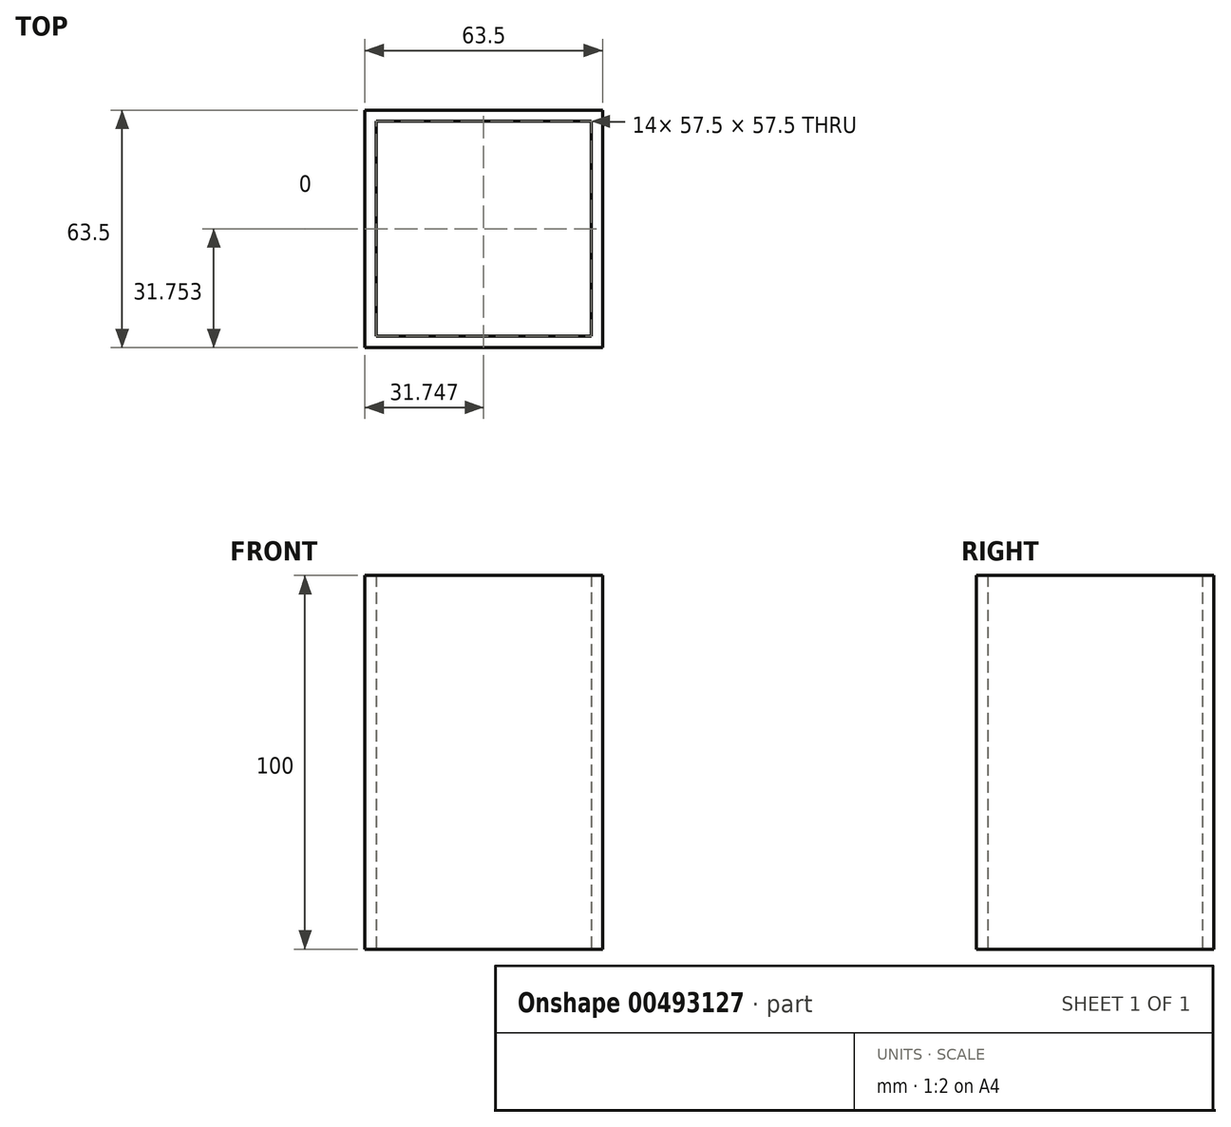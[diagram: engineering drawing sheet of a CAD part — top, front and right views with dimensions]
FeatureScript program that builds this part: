
annotation { "Feature Type Name" : "Feature", "Feature Type Description" : "" }
export const myFeature = defineFeature(function(context is Context, id is Id, definition is map)
    precondition{}
    {
        {
            var Q0;
            Q0=qCreatedBy(makeId("Top.planeOp"),FACE);
            var sketch = newSketch(context, id + "F0", { "sketchPlane" : qUnion([Q0])});
            skLineSegment(sketch, "E0.bottom", {"start": v(-27.63, 16.07) * mm, "end": v(29.87, 16.07) * mm});
            skLineSegment(sketch, "E0.top", {"start": v(-27.63, -41.43) * mm, "end": v(29.87, -41.43) * mm});
            skLineSegment(sketch, "E0.left", {"start": v(-27.63, 16.07) * mm, "end": v(-27.63, -41.43) * mm});
            skLineSegment(sketch, "E0.right", {"start": v(29.87, 16.07) * mm, "end": v(29.87, -41.43) * mm});
            skLineSegment(sketch, "E1.bottom", {"start": v(-30.63, 19.07) * mm, "end": v(32.87, 19.07) * mm});
            skLineSegment(sketch, "E1.top", {"start": v(-30.63, -44.43) * mm, "end": v(32.87, -44.43) * mm});
            skLineSegment(sketch, "E1.left", {"start": v(-30.63, 19.07) * mm, "end": v(-30.63, -44.43) * mm});
            skLineSegment(sketch, "E1.right", {"start": v(32.87, 19.07) * mm, "end": v(32.87, -44.43) * mm});
            skSolve(sketch);
        }
        {
            var Q0;
            Q0=qSketchRegion(id+"F0",true);
            extrude(context, id + "F1", {"entities" : qUnion([Q0]), "depth" : 100 * mm});
        }
    });
